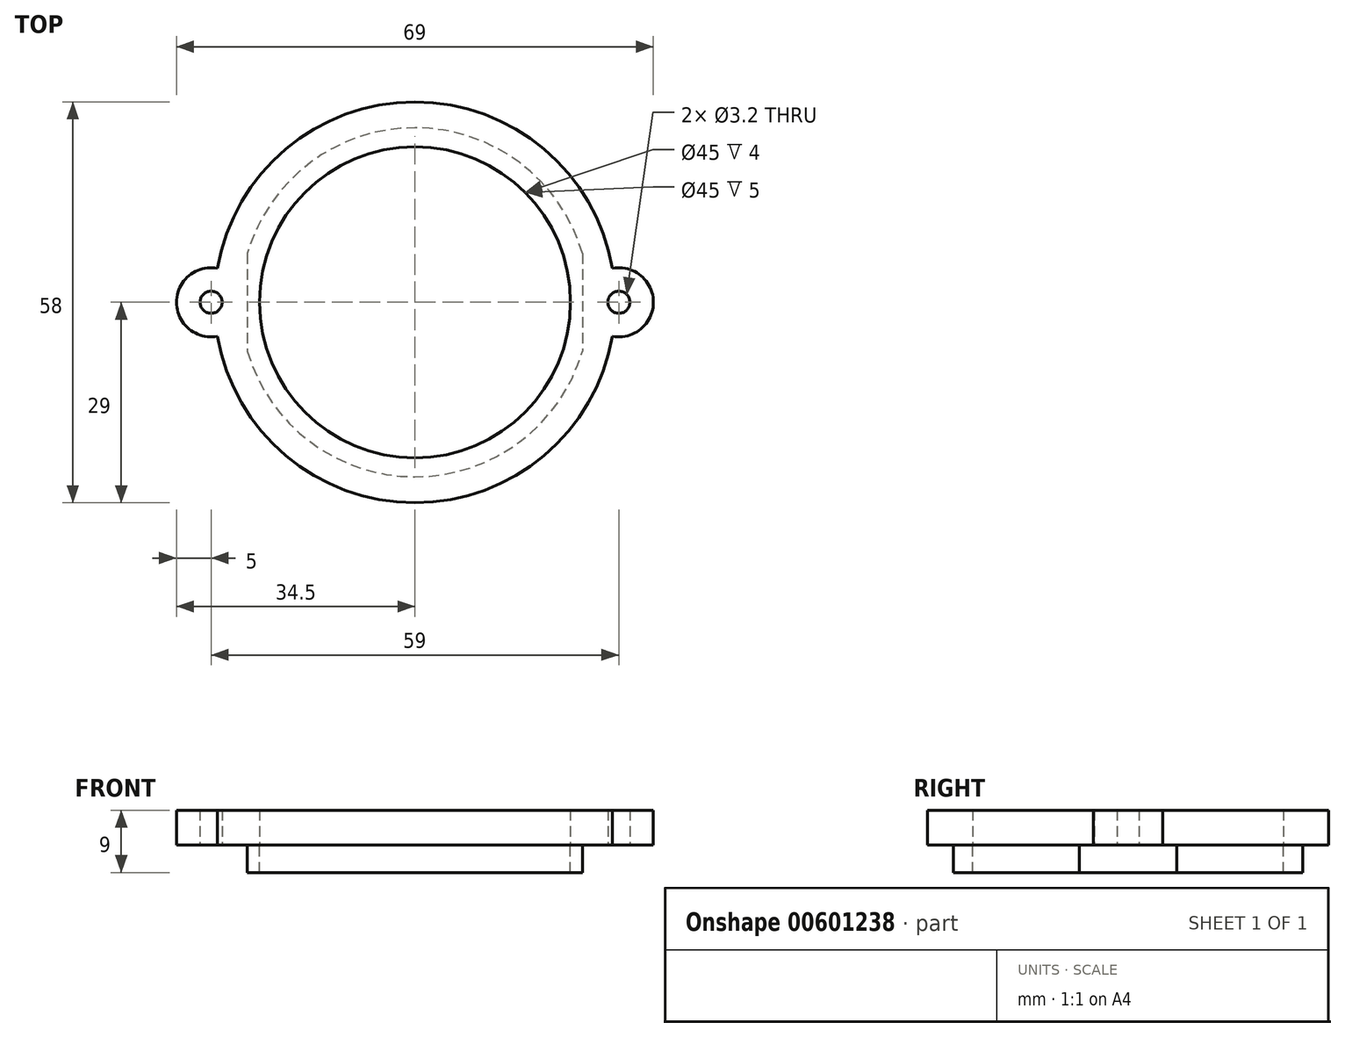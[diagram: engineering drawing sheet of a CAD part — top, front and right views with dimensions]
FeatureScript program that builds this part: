
annotation { "Feature Type Name" : "Feature", "Feature Type Description" : "" }
export const myFeature = defineFeature(function(context is Context, id is Id, definition is map)
    precondition{}
    {
        {
            var Q0;
            Q0=qCreatedBy(makeId("Top.planeOp"),FACE);
            var sketch = newSketch(context, id + "F0", { "sketchPlane" : qUnion([Q0])});
            skArc(sketch, "E0", {"start": v(24.24, 7.07) * mm, "mid": v(0, 25.25) * mm, "end": v(-24.24, 7.07) * mm});
            skLineSegment(sketch, "E1.left", {"start": v(-24.24, 7.07) * mm, "end": v(-24.24, -7.07) * mm});
            skLineSegment(sketch, "E1.right", {"start": v(24.24, 7.07) * mm, "end": v(24.24, -7.07) * mm});
            skArc(sketch, "E2.trimOffspring", {"start": v(-24.24, -7.07) * mm, "mid": v(0, -25.25) * mm, "end": v(24.24, -7.07) * mm});
            skPoint(sketch, "E3.centerSnap0", {"position": v(0, -25.25) * mm});
            skCircle(sketch, "E4", {"center": v(0, 0) * mm, "radius": 22.5 * mm});
            skCircle(sketch, "E5", {"center": v(0, 0) * mm, "radius": 29 * mm});
            skCircle(sketch, "E6", {"center": v(-29.5, 0) * mm, "radius": 5 * mm});
            skCircle(sketch, "E7", {"center": v(29.5, 0) * mm, "radius": 5 * mm});
            skCircle(sketch, "E8", {"center": v(-29.5, 0) * mm, "radius": 1.6 * mm});
            skCircle(sketch, "E9", {"center": v(29.5, 0) * mm, "radius": 1.6 * mm});
            skSolve(sketch);
        }
        {
            var Q0;
            {var subQ0=sQuery(id+"F0.wireOp",EDGE,"E6");var subQ1=sQuery(id+"F0.wireOp",EDGE,"E5");var subQ2=makeQuery(id+"F0.imprint","INTERSECT",VERTEX,{"disambiguationData":[OD(0.0)],"derivedFrom":[subQ1,subQ0]});Q0=makeQuery(id+"F0.imprint","IMPRINT",FACE,{"disambiguationData":[TD([[makeQuery(id+"F0.imprint","IMPRINT",EDGE,{"disambiguationData":[TD([[subQ2,-1.0]])],"derivedFrom":subQ1}),-1.0]])]});}
            var Q1;
            {var subQ0=sQuery(id+"F0.wireOp",EDGE,"E6");var subQ5=sQuery(id+"F0.wireOp",EDGE,"E1.left");var subQ6=makeQuery(id+"F0.imprint","INTERSECT",VERTEX,{"disambiguationData":[OD(0.0)],"derivedFrom":[subQ5,subQ0]});Q1=makeQuery(id+"F0.imprint","IMPRINT",FACE,{"disambiguationData":[TD([[makeQuery(id+"F0.imprint","IMPRINT",EDGE,{"disambiguationData":[TD([[subQ6,-1.0]])],"derivedFrom":subQ5}),-1.0]])]});}
            var Q2;
            {var subQ1=sQuery(id+"F0.wireOp",EDGE,"E0");Q2=makeQuery(id+"F0.imprint","IMPRINT",FACE,{"disambiguationData":[TD([[makeQuery(id+"F0.imprint","IMPRINT",EDGE,{"derivedFrom":subQ1}),-1.0]])]});}
            var Q3;
            {var subQ1=sQuery(id+"F0.wireOp",EDGE,"E0");Q3=makeQuery(id+"F0.imprint","IMPRINT",FACE,{"disambiguationData":[TD([[makeQuery(id+"F0.imprint","IMPRINT",EDGE,{"derivedFrom":subQ1}),1.0]])]});}
            var Q4;
            {var subQ5=sQuery(id+"F0.wireOp",EDGE,"E2.trimOffspring");Q4=makeQuery(id+"F0.imprint","IMPRINT",FACE,{"disambiguationData":[TD([[makeQuery(id+"F0.imprint","IMPRINT",EDGE,{"derivedFrom":subQ5}),-1.0]])]});}
            var Q5;
            {var subQ0=sQuery(id+"F0.wireOp",EDGE,"E7");var subQ3=sQuery(id+"F0.wireOp",EDGE,"E1.right");var subQ4=makeQuery(id+"F0.imprint","INTERSECT",VERTEX,{"disambiguationData":[OD(0.0)],"derivedFrom":[subQ3,subQ0]});Q5=makeQuery(id+"F0.imprint","IMPRINT",FACE,{"disambiguationData":[TD([[makeQuery(id+"F0.imprint","IMPRINT",EDGE,{"disambiguationData":[TD([[subQ4,-1.0]])],"derivedFrom":subQ3}),1.0]])]});}
            var Q6;
            {var subQ0=sQuery(id+"F0.wireOp",EDGE,"E7");var subQ1=sQuery(id+"F0.wireOp",EDGE,"E5");var subQ2=makeQuery(id+"F0.imprint","INTERSECT",VERTEX,{"disambiguationData":[OD(0.0)],"derivedFrom":[subQ1,subQ0]});Q6=makeQuery(id+"F0.imprint","IMPRINT",FACE,{"disambiguationData":[TD([[makeQuery(id+"F0.imprint","IMPRINT",EDGE,{"disambiguationData":[TD([[subQ2,1.0]])],"derivedFrom":subQ1}),-1.0]])]});}
            var Q7;
            {var subQ0=sQuery(id+"F0.wireOp",EDGE,"E6");var subQ1=sQuery(id+"F0.wireOp",EDGE,"E5");var subQ2=makeQuery(id+"F0.imprint","INTERSECT",VERTEX,{"disambiguationData":[OD(0.0)],"derivedFrom":[subQ1,subQ0]});Q7=makeQuery(id+"F0.imprint","IMPRINT",FACE,{"disambiguationData":[TD([[makeQuery(id+"F0.imprint","IMPRINT",EDGE,{"disambiguationData":[TD([[subQ2,-1.0]])],"derivedFrom":subQ1}),1.0]])]});}
            var Q8;
            {var subQ0=sQuery(id+"F0.wireOp",EDGE,"E7");var subQ1=sQuery(id+"F0.wireOp",EDGE,"E5");var subQ2=makeQuery(id+"F0.imprint","INTERSECT",VERTEX,{"disambiguationData":[OD(0.0)],"derivedFrom":[subQ1,subQ0]});Q8=makeQuery(id+"F0.imprint","IMPRINT",FACE,{"disambiguationData":[TD([[makeQuery(id+"F0.imprint","IMPRINT",EDGE,{"disambiguationData":[TD([[subQ2,1.0]])],"derivedFrom":subQ1}),1.0]])]});}
            extrude(context, id + "F1", {"entities" : qUnion([Q0, Q1, Q2, Q3, Q4, Q5, Q6, Q7, Q8]), "depth" : 5 * mm, "offsetDistance" : 25 * mm});
        }
        {
            var Q0;
            {var subQ1=sQuery(id+"F0.wireOp",EDGE,"E0");Q0=makeQuery(id+"F0.imprint","IMPRINT",FACE,{"disambiguationData":[TD([[makeQuery(id+"F0.imprint","IMPRINT",EDGE,{"derivedFrom":subQ1}),1.0]])]});}
            extrude(context, id + "F2", {"entities" : qUnion([Q0]), "oppositeDirection" : true, "depth" : 4 * mm, "offsetDistance" : 25 * mm});
        }
    });
